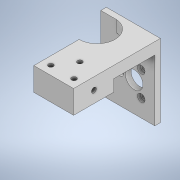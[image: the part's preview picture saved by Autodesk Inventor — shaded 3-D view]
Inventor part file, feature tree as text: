
AUTODESK INVENTOR PART (.ipt)
format: ipt  version: 2021 (Build 250183000, 183)  size: 283,136 bytes
history: native  units: mm
features: extrude x16, sketch x16, projected_geometry x10, plane x1
ambient origin geometry x8: Origin, YZ Plane, XZ Plane, XY Plane, X Axis, Y Axis, Z Axis, Center Point
bodies: Solid1 (feature_tree)
feature tree (43):
  plane  "Work Plane1"
  extrude  "Extrusion1"  Depth=5.0mm TaperAngle=0.0deg
  extrude  "Extrusion2"  Depth=5.0mm TaperAngle=0.0deg
  extrude  "Extrusion3"  Depth=75.0mm
  extrude  "Extrusion4"  Depth=15.0mm
  extrude  "Extrusion5"  Depth=8.5mm
  extrude  "Extrusion6"  Depth=20.0mm TaperAngle=0.0deg
  extrude  "Extrusion7"  Depth=20.0mm TaperAngle=0.0deg
  extrude  "Extrusion10"  Depth=10.0mm
  extrude  "Extrusion11"  Depth=20.0mm TaperAngle=0.0deg
  extrude  "Extrusion12"  Depth=40.0mm
  extrude  "Extrusion13"  Depth=30.0mm TaperAngle=0.0deg
  extrude  "Extrusion14"  Depth=35.0mm
  extrude  "Extrusion15"  TaperAngle=0.0deg  [1 undecoded]
  extrude  "Extrusion16"  Depth=20.0mm
  extrude  "Extrusion17"  Depth=10.0mm TaperAngle=0.0deg
  extrude  "Extrusion18"  Depth=10.0mm
  sketch  "Sketch1"  dims[d3=30.0mm d4=5.0mm d5=0.0mm]
  sketch  "Sketch2"  dims[d6=5.0mm d7=0.0mm d8=5.0mm d9=0.0mm]
  projected_geometry  "Projected Loop1"
  sketch  "Sketch3"  dims[d12=75.0mm d13=0.0mm d14=14.25mm]
  projected_geometry  "Projected Loop2"
  sketch  "Sketch4"  dims[d15=40.0mm d16=15.0mm]
  sketch  "Sketch5"  dims[d17=8.5mm d18=8.5mm]
  sketch  "Sketch6"  dims[d19=0.0mm d20=0.0mm d22=20.0mm d23=0.0mm]
  projected_geometry  "Projected Loop3"
  sketch  "Sketch7"  dims[d24=20.0mm d25=0.0mm d31=65.718mm d32=0.0mm]
  projected_geometry  "Projected Loop4"
  projected_geometry  "Projected Loop5"
  sketch  "Sketch10"  dims[d33=10.0mm d34=0.0mm d35=10.0mm]
  projected_geometry  "Projected Loop8"
  sketch  "Sketch11"  dims[d36=20.0mm d37=0.0mm d39=59.488mm d40=0.0mm]
  projected_geometry  "Projected Loop9"
  sketch  "Sketch12"  dims[d43=40.0mm d44=8.5mm]
  sketch  "Sketch13"  dims[d45=8.5mm d46=30.0mm d47=0.0mm]
  projected_geometry  "Projected Loop10"
  sketch  "Sketch14"  dims[d48=1.0mm d49=0.0mm d50=35.0mm]
  sketch  "Sketch15"  dims[d51=8.5mm d52=0.0mm d53=0.0mm]
  projected_geometry  "Projected Loop11"
  sketch  "Sketch16"  dims[d54=20.0mm d55=30.0mm]
  sketch  "Sketch17"  dims[d56=8.5mm d57=10.0mm d58=0.0mm]
  sketch  "Sketch18"  dims[d59=13.0mm d60=13.0mm d61=13.0mm d62=10.0mm d63=0.0mm]
  projected_geometry  "Projected Loop12"
note: 1 required parameter value undecoded (feature->parameter linkage not recoverable at this tier; creation-order binding heuristic only, values carry confidence <= 0.55)
